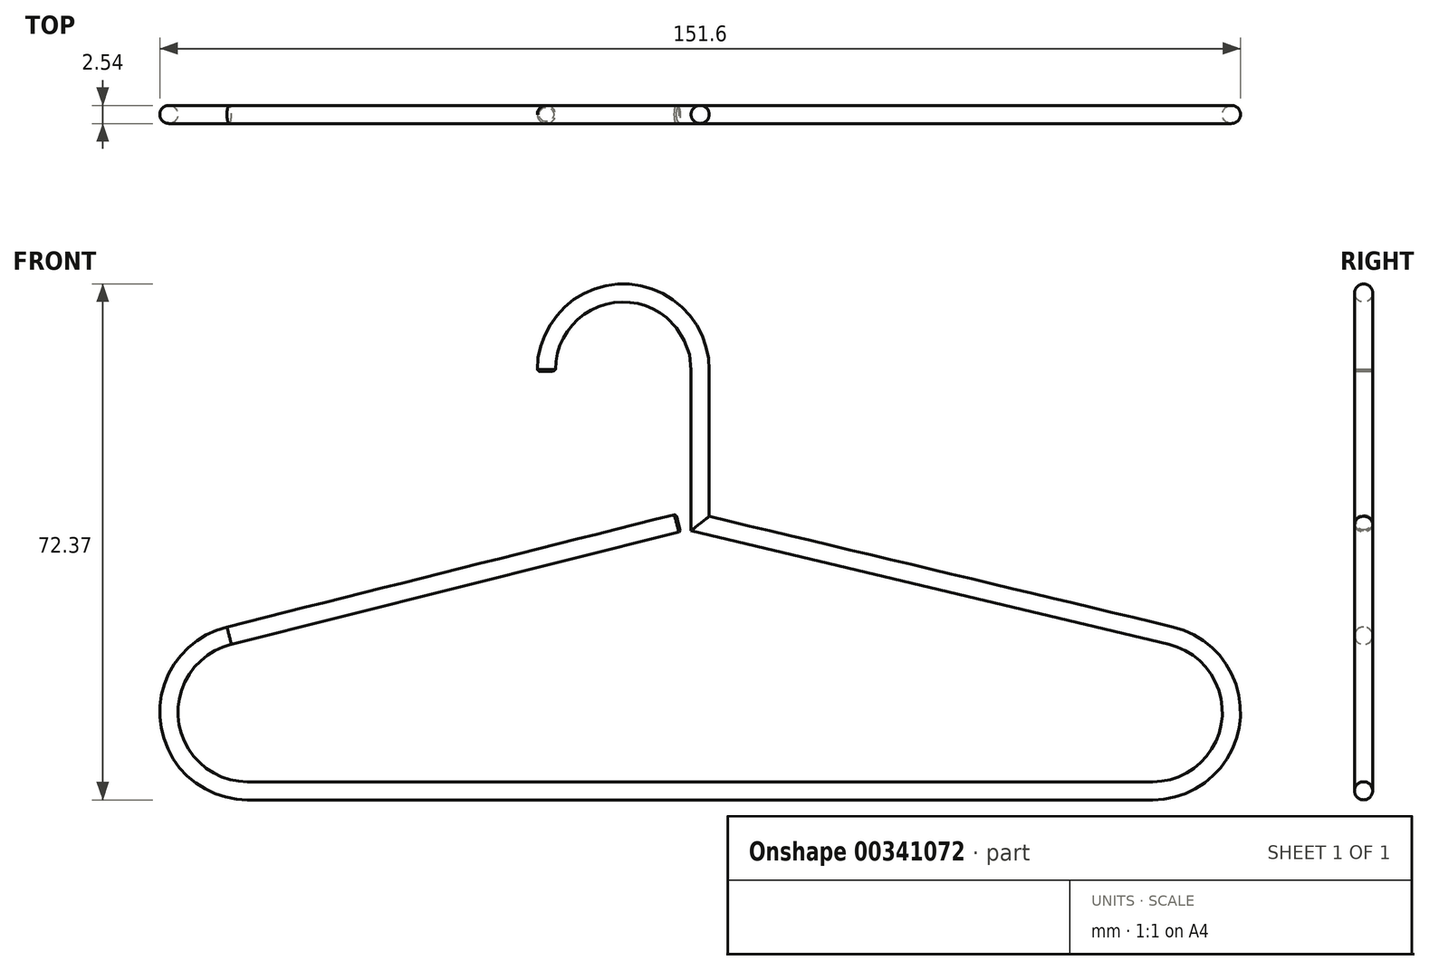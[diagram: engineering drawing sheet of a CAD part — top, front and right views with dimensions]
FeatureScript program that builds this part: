
annotation { "Feature Type Name" : "Feature", "Feature Type Description" : "" }
export const myFeature = defineFeature(function(context is Context, id is Id, definition is map)
    precondition{}
    {
        {
            var Q0;
            Q0=qCreatedBy(makeId("Front.planeOp"),FACE);
            var sketch = newSketch(context, id + "F0", { "sketchPlane" : qUnion([Q0])});
            skLineSegment(sketch, "E0", {"start": v(0, 0) * mm, "end": v(63.5, 0) * mm});
            skArc(sketch, "E1", {"start": v(63.5, 0) * mm, "mid": v(74.45, 9.74) * mm, "end": v(66.06, 21.75) * mm});
            skLineSegment(sketch, "E2", {"start": v(66.06, 21.75) * mm, "end": v(0, 37.5) * mm});
            skLineSegment(sketch, "E3", {"start": v(0, 37.5) * mm, "end": v(0, 59.04) * mm});
            skArc(sketch, "E4", {"start": v(0, 59.04) * mm, "mid": v(-10.88, 69.82) * mm, "end": v(-21.56, 58.85) * mm});
            skSolve(sketch);
        }
        {
            var Q0;
            Q0=qCreatedBy(makeId("Right.planeOp"),FACE);
            var sketch = newSketch(context, id + "F1", { "sketchPlane" : qUnion([Q0])});
            skCircle(sketch, "E5", {"center": v(0, 0) * mm, "radius": 1.27 * mm});
            skSolve(sketch);
        }
        {
            var Q0;
            Q0 = qSketchRegion(id + "F1", true);
            var Q1;
            Q1 = qConstructionFilter(qBodyType(qCreatedBy(id + "F0" ,EDGE), BodyType.WIRE), ConstructionObject.NO);
            sweep(context, id + "F2", {"profiles" : qUnion([Q0]), "path" : qUnion([Q1])});
        }
        {
            var Q0;
            Q0=qCreatedBy(makeId("Front.planeOp"),FACE);
            var sketch = newSketch(context, id + "F3", { "sketchPlane" : qUnion([Q0])});
            skLineSegment(sketch, "E6", {"start": v(0, 0) * mm, "end": v(-63.5, 0) * mm});
            skArc(sketch, "E7.MirrorCS", {"start": v(-63.5, 0) * mm, "mid": v(-74.45, 9.74) * mm, "end": v(-66.06, 21.75) * mm});
            skLineSegment(sketch, "E8", {"start": v(-66.06, 21.75) * mm, "end": v(-3.06, 37.57) * mm});
            skSolve(sketch);
        }
        {
            var Q0;
            Q0=qCreatedBy(makeId("Right.planeOp"),FACE);
            var sketch = newSketch(context, id + "F4", { "sketchPlane" : qUnion([Q0])});
            skCircle(sketch, "E9", {"center": v(0, 0) * mm, "radius": 1.27 * mm});
            skSolve(sketch);
        }
        {
            var Q0;
            Q0 = qSketchRegion(id + "F4", true);
            var Q1;
            Q1 = qConstructionFilter(qBodyType(qCreatedBy(id + "F3" ,EDGE), BodyType.WIRE), ConstructionObject.NO);
            sweep(context, id + "F5", {"operationType" : NewBodyOperationType.ADD, "profiles" : qUnion([Q0]), "path" : qUnion([Q1])});
        }
        {
            var Q0;
            Q0=makeQuery(id+"F2.opSweep","CAP_FACE",FACE,{"disambiguationData":[OSD([sQuery(id+"F0.wireOp",VERTEX,"E4.end"),sQuery(id+"F1.wireOp",EDGE,"E5")])],"isStart":false});
            chamfer(context, id + "F6", {"entities" : qUnion([Q0]), "width" : 0.25 * mm, "tangentPropagation" : true});
        }
        {
            var Q0;
            Q0=makeQuery(id+"F5.opSweep","CAP_EDGE",EDGE,{"disambiguationData":[OSD([sQuery(id+"F3.wireOp",VERTEX,"E8.end"),sQuery(id+"F4.wireOp",EDGE,"E9")])],"isStart":false});
            chamfer(context, id + "F7", {"entities" : qUnion([Q0]), "width" : 0.25 * mm, "tangentPropagation" : true});
        }
    });
